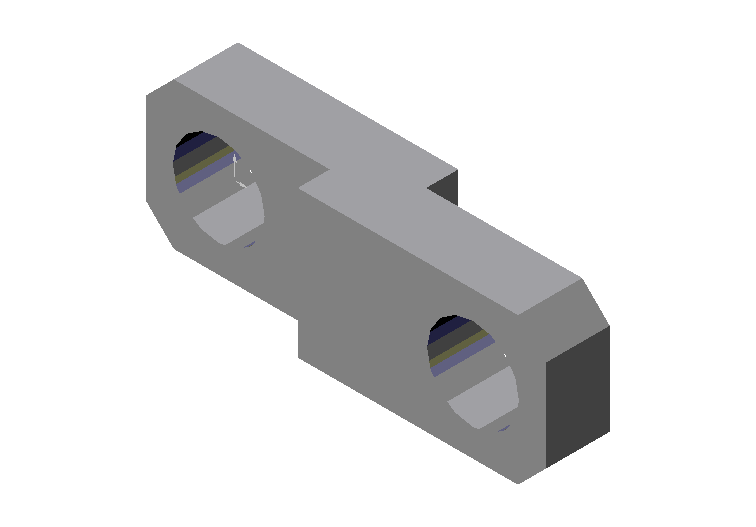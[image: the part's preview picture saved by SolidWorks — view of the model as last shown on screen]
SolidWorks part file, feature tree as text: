
SOLIDWORKS PART (.sldprt)
format: sldprt  version: not decoded by parser v0  size: 125,440 bytes
history: native  units: mm
features: plane x3, sketch x3, cut_extrude x2, material x1, extrude x1, chamfer x1 (+8 scaffold rows collapsed)
feature tree (19):
  scaffold x8  (default folders/planes/origin — collapsed)
  material  "Matériau <non spécifié>"
  plane  "Face"
  plane  "Dessus"
  plane  "Droite"
  sketch  "Esquisse1"  dims[c1.D1=8.0mm c1.D2=5.0mm c2.D1=15.6mm c2.D3=27.0mm c3.D1=15.6mm c3.D3=23.5mm c3.D4=8.0mm]
  extrude  "Base-Extrusion"  Depth=5.25mm
  sketch  "Esquisse2"  dims[c1.D1=10.0mm c1.D2=2.0mm c1.D3=~2.864001mm c2.D3=30.0deg c2.D4=0.0mm]
  cut_extrude  "Enlèv. mat.-Extru.1"  Depth=1.75mm
  sketch  "Esquisse3"  dims[c1.D1=10.0mm c1.D2=2.0mm c1.D3=~4.074617mm c2.D3=30.0deg c2.D4=0.0mm]
  cut_extrude  "Enlèv. mat.-Extru.2"  Depth=1.75mm
  chamfer  "Chanfrein1"  Distance=1.5mm Angle=45deg
decode coverage: 7 of 7 modeling features carry decoded parameters
note: ~ marks probable driven/reference dimensions
note: suppression state not decoded; provenance and decode notes live in map.json
